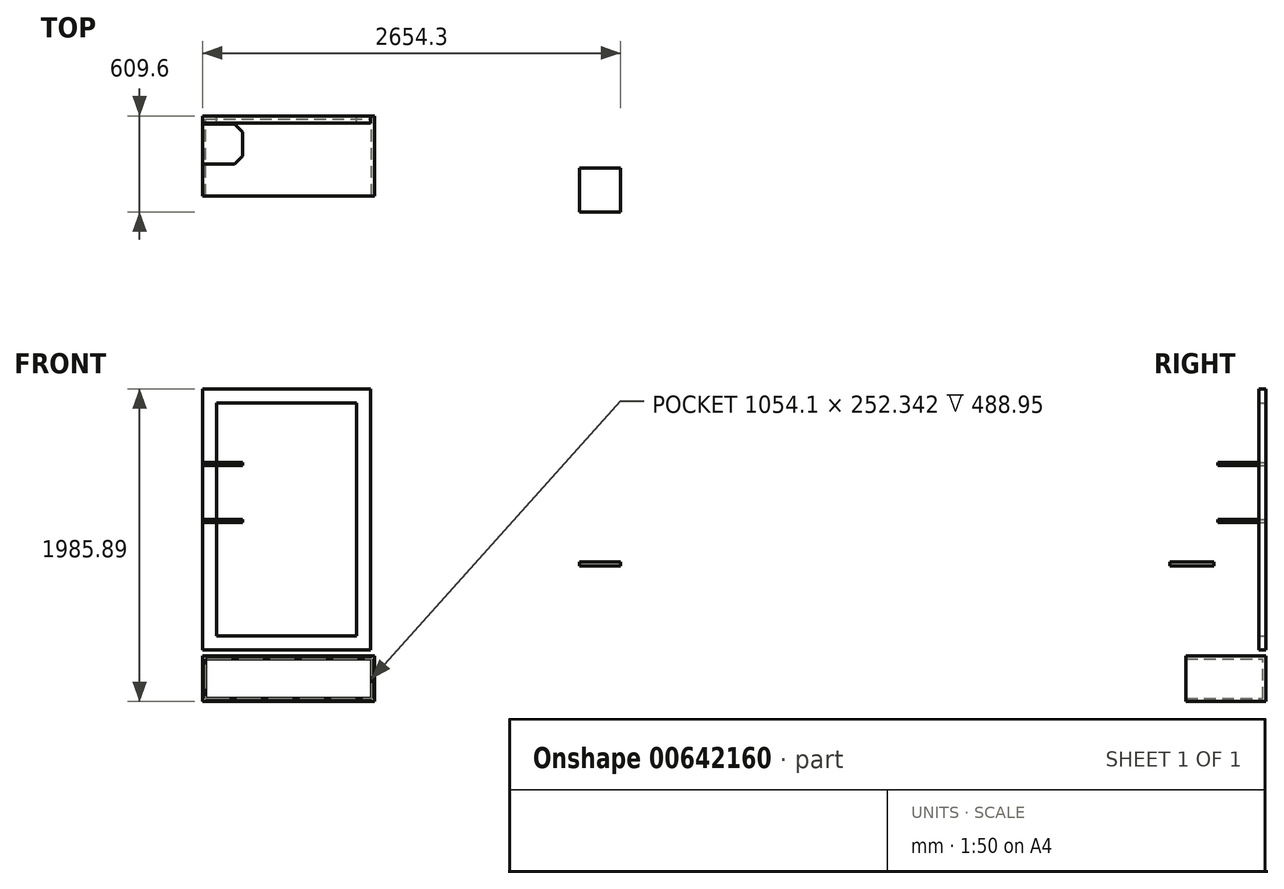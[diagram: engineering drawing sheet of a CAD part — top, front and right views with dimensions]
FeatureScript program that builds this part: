
annotation { "Feature Type Name" : "Feature", "Feature Type Description" : "" }
export const myFeature = defineFeature(function(context is Context, id is Id, definition is map)
    precondition{}
    {
        {
            var Q0;
            Q0=qCreatedBy(makeId("Front.planeOp"),FACE);
            var sketch = newSketch(context, id + "F0", { "sketchPlane" : qUnion([Q0])});
            skLineSegment(sketch, "E0.bottom", {"start": v(0, 0) * mm, "end": v(2654.3, 0) * mm});
            skLineSegment(sketch, "E0.top", {"start": v(0, 2432.05) * mm, "end": v(2654.3, 2432.05) * mm});
            skLineSegment(sketch, "E0.left", {"start": v(0, 0) * mm, "end": v(0, 2432.05) * mm});
            skLineSegment(sketch, "E0.right", {"start": v(2654.3, 0) * mm, "end": v(2654.3, 2432.05) * mm});
            skLineSegment(sketch, "E1.bottom", {"start": v(0, 495.3) * mm, "end": v(1066.8, 495.3) * mm});
            skLineSegment(sketch, "E1.top", {"start": v(0, 2152.65) * mm, "end": v(1066.8, 2152.65) * mm});
            skLineSegment(sketch, "E1.left", {"start": v(0, 495.3) * mm, "end": v(0, 2152.65) * mm});
            skLineSegment(sketch, "E1.right", {"start": v(1066.8, 495.3) * mm, "end": v(1066.8, 2152.65) * mm});
            skLineSegment(sketch, "E2.bottom", {"start": v(2654.3, 1029.79) * mm, "end": v(2393.58, 1029.79) * mm});
            skLineSegment(sketch, "E2.top", {"start": v(2654.3, 1065.5) * mm, "end": v(2393.58, 1065.5) * mm});
            skLineSegment(sketch, "E2.left", {"start": v(2654.3, 1029.79) * mm, "end": v(2654.3, 1065.5) * mm});
            skLineSegment(sketch, "E2.right", {"start": v(2393.58, 1029.79) * mm, "end": v(2393.58, 1065.5) * mm});
            skLineSegment(sketch, "E3.bottom", {"start": v(0, 0) * mm, "end": v(1092.2, 0) * mm});
            skLineSegment(sketch, "E3.top", {"start": v(0, 457.2) * mm, "end": v(1092.2, 457.2) * mm});
            skLineSegment(sketch, "E3.left", {"start": v(0, 0) * mm, "end": v(0, 457.2) * mm});
            skLineSegment(sketch, "E3.right", {"start": v(1092.2, 0) * mm, "end": v(1092.2, 457.2) * mm});
            skLineSegment(sketch, "E4", {"start": v(0, 166.76) * mm, "end": v(1092.2, 166.76) * mm});
            skLineSegment(sketch, "E5", {"start": v(1092.2, 0) * mm, "end": v(1092.2, 914.4) * mm});
            skLineSegment(sketch, "E6", {"start": v(1574.8, 1244.6) * mm, "end": v(1574.8, 0) * mm});
            skLineSegment(sketch, "E7", {"start": v(1981.2, 914.4) * mm, "end": v(1981.2, 0) * mm});
            skLineSegment(sketch, "E8", {"start": v(1574.8, 914.4) * mm, "end": v(1981.2, 914.4) * mm});
            skLineSegment(sketch, "E9", {"start": v(1574.8, 914.4) * mm, "end": v(1092.2, 914.4) * mm});
            skLineSegment(sketch, "E10", {"start": v(1092.2, 101.6) * mm, "end": v(1981.2, 101.6) * mm});
            skLineSegment(sketch, "E11", {"start": v(1981.2, 482.6) * mm, "end": v(2590.8, 482.6) * mm});
            skLineSegment(sketch, "E12", {"start": v(1981.2, 1054.41) * mm, "end": v(2590.8, 1054.41) * mm});
            skLineSegment(sketch, "E13", {"start": v(2590.8, 1054.41) * mm, "end": v(2654.3, 1054.41) * mm});
            skLineSegment(sketch, "E14.trimOffspring", {"start": v(2590.8, 1054.41) * mm, "end": v(2590.8, 0) * mm});
            skLineSegment(sketch, "E15", {"start": v(1574.8, 533.4) * mm, "end": v(1092.2, 533.4) * mm});
            skLineSegment(sketch, "E16", {"start": v(1981.2, 914.4) * mm, "end": v(1981.2, 1054.41) * mm});
            skLineSegment(sketch, "E17", {"start": v(1574.8, 1244.6) * mm, "end": v(1981.2, 1244.6) * mm});
            skLineSegment(sketch, "E18", {"start": v(1981.2, 1244.6) * mm, "end": v(1981.2, 1054.41) * mm});
            skLineSegment(sketch, "E19.bottom", {"start": v(0, 1687.02) * mm, "end": v(254, 1687.02) * mm});
            skLineSegment(sketch, "E19.top", {"start": v(0, 1667.97) * mm, "end": v(254, 1667.97) * mm});
            skLineSegment(sketch, "E19.left", {"start": v(0, 1687.02) * mm, "end": v(0, 1667.97) * mm});
            skLineSegment(sketch, "E19.right", {"start": v(254, 1687.02) * mm, "end": v(254, 1667.97) * mm});
            skLineSegment(sketch, "E20.bottom", {"start": v(0, 1323.98) * mm, "end": v(254, 1323.98) * mm});
            skLineSegment(sketch, "E20.top", {"start": v(0, 1304.93) * mm, "end": v(254, 1304.93) * mm});
            skLineSegment(sketch, "E20.left", {"start": v(0, 1323.98) * mm, "end": v(0, 1304.93) * mm});
            skLineSegment(sketch, "E20.right", {"start": v(254, 1323.98) * mm, "end": v(254, 1304.93) * mm});
            skLineSegment(sketch, "E21", {"start": v(1574.8, 355.6) * mm, "end": v(1981.2, 355.6) * mm});
            skLineSegment(sketch, "E22", {"start": v(88.9, 2063.75) * mm, "end": v(88.9, 584.2) * mm});
            skLineSegment(sketch, "E23", {"start": v(88.9, 2063.75) * mm, "end": v(977.9, 2063.75) * mm});
            skLineSegment(sketch, "E24", {"start": v(977.9, 2063.75) * mm, "end": v(977.9, 584.2) * mm});
            skLineSegment(sketch, "E25", {"start": v(88.9, 584.2) * mm, "end": v(977.9, 584.2) * mm});
            skSolve(sketch);
        }
        {
            var Q0;
            {var subQ4=sQuery(id+"F0.wireOp",EDGE,"E3.top");Q0=makeQuery(id+"F0.imprint","IMPRINT",FACE,{"disambiguationData":[TD([[makeQuery(id+"F0.imprint","IMPRINT",EDGE,{"derivedFrom":subQ4}),-1.0]])]});}
            extrude(context, id + "F1", {"entities" : qUnion([Q0]), "depth" : 508 * mm, "offsetDistance" : 25.4 * mm});
        }
        {
            var Q0;
            Q0=sQuery(id+"F0.wireOp",EDGE,"E5");
            var Q1;
            Q1=sQuery(id+"F0.wireOp",EDGE,"E6");
            var Q2;
            Q2=sQuery(id+"F0.wireOp",EDGE,"E16");
            var Q3;
            Q3=sQuery(id+"F0.wireOp",EDGE,"E7");
            var Q4;
            Q4=sQuery(id+"F0.wireOp",EDGE,"E14.trimOffspring");
            var Q5;
            Q5=sQuery(id+"F0.wireOp",EDGE,"E18");
            var Q6;
            Q6=sQuery(id+"F0.wireOp",EDGE,"sEqqkKkJ-zDKM-WJjd-21iw-gBiEN16Gd99Q");
            extrude(context, id + "F2", {"bodyType" : ToolBodyType.SURFACE, "surfaceEntities" : qUnion([Q0, Q1, Q2, Q3, Q4, Q5, Q6]), "depth" : 355.6 * mm, "offsetDistance" : 25.4 * mm});
        }
        {
            var Q0;
            Q0=sQuery(id+"F0.wireOp",EDGE,"Kjtz5eKt-ULTf-evfQ-Q5N2-FUeb1anu7QRw");
            var Q1;
            Q1=sQuery(id+"F0.wireOp",EDGE,"E9");
            var Q2;
            Q2=sQuery(id+"F0.wireOp",EDGE,"E8");
            var Q3;
            Q3=sQuery(id+"F0.wireOp",EDGE,"E12");
            var Q4;
            Q4=sQuery(id+"F0.wireOp",EDGE,"E11");
            var Q5;
            Q5=sQuery(id+"F0.wireOp",EDGE,"0XJa6nW8-y0aG-1m5H-tmE6-vHsM1P7Ta5Jt");
            var Q6;
            Q6=sQuery(id+"F0.wireOp",EDGE,"E15");
            var Q7;
            Q7=sQuery(id+"F0.wireOp",EDGE,"E10");
            var Q8;
            Q8=sQuery(id+"F0.wireOp",EDGE,"E17");
            var Q9;
            Q9=sQuery(id+"F0.wireOp",EDGE,"MFajBvlE-Buub-MDIa-xRfk-fOyj7VufqCmV");
            var Q10;
            Q10=sQuery(id+"F0.wireOp",EDGE,"E21");
            extrude(context, id + "F3", {"bodyType" : ToolBodyType.SURFACE, "surfaceEntities" : qUnion([Q0, Q1, Q2, Q3, Q4, Q5, Q6, Q7, Q8, Q9, Q10]), "depth" : 355.6 * mm, "offsetDistance" : 25.4 * mm});
        }
        {
            var Q0;
            Q0=sQuery(id+"F0.wireOp",EDGE,"E0.left");
            extrude(context, id + "F4", {"bodyType" : ToolBodyType.SURFACE, "surfaceEntities" : qUnion([Q0]), "depth" : 419.1 * mm, "offsetDistance" : 25.4 * mm});
        }
        {
            var Q0;
            Q0=sQuery(id+"F0.wireOp",EDGE,"E0.right");
            extrude(context, id + "F5", {"bodyType" : ToolBodyType.SURFACE, "surfaceEntities" : qUnion([Q0]), "depth" : 355.6 * mm, "offsetDistance" : 25.4 * mm});
        }
        {
            var Q0;
            Q0=makeQuery(id+"F0.imprint","IMPRINT",FACE,{"disambiguationData":[TD([[makeQuery(id+"F0.imprint","IMPRINT",EDGE,{"derivedFrom":sQuery(id+"F0.wireOp",EDGE,"E2.bottom")}),-1.0]])]});
            extrude(context, id + "F6", {"entities" : qUnion([Q0]), "depth" : 609.6 * mm, "offsetDistance" : 25.4 * mm, "hasSecondDirection" : true, "secondDirectionOppositeDirection" : false, "secondDirectionDepth" : 330.2 * mm});
        }
        {
            var Q0;
            Q0=makeQuery(id+"F0.imprint","IMPRINT",FACE,{"disambiguationData":[TD([[makeQuery(id+"F0.imprint","IMPRINT",EDGE,{"derivedFrom":sQuery(id+"F0.wireOp",EDGE,"E19.bottom")}),-1.0]])]});
            var Q1;
            Q1=makeQuery(id+"F0.imprint","IMPRINT",FACE,{"disambiguationData":[TD([[makeQuery(id+"F0.imprint","IMPRINT",EDGE,{"derivedFrom":sQuery(id+"F0.wireOp",EDGE,"E20.bottom")}),-1.0]])]});
            extrude(context, id + "F7", {"entities" : qUnion([Q0, Q1]), "depth" : 304.8 * mm, "offsetDistance" : 25.4 * mm, "hasSecondDirection" : true, "secondDirectionOppositeDirection" : false, "secondDirectionDepth" : 50.8 * mm});
        }
        {
            var Q0;
            Q0=makeQuery(id+"F7.opExtrude","CAP_EDGE",EDGE,{"disambiguationData":[OSD([sQuery(id+"F0.wireOp",EDGE,"E19.right")])],"isStart":false});
            var Q1;
            Q1=makeQuery(id+"F7.opExtrude","CAP_EDGE",EDGE,{"disambiguationData":[OSD([sQuery(id+"F0.wireOp",EDGE,"E20.right")])],"isStart":false});
            var Q2;
            Q2=makeQuery(id+"F7.opExtrude","CAP_EDGE",EDGE,{"disambiguationData":[OSD([sQuery(id+"F0.wireOp",EDGE,"E19.right")])],"isStart":true});
            var Q3;
            Q3=makeQuery(id+"F7.opExtrude","CAP_EDGE",EDGE,{"disambiguationData":[OSD([sQuery(id+"F0.wireOp",EDGE,"E20.right")])],"isStart":true});
            chamfer(context, id + "F8", {"entities" : qUnion([Q0, Q1, Q2, Q3]), "width" : 50.8 * mm, "tangentPropagation" : true});
        }
        {
            var Q0;
            {var subQ0=sQuery(id+"F0.wireOp",EDGE,"E20.left");Q0=makeQuery(id+"F0.imprint","IMPRINT",FACE,{"disambiguationData":[TD([[makeQuery(id+"F0.imprint","IMPRINT",EDGE,{"derivedFrom":subQ0}),1.0]])]});}
            var Q1;
            {var subQ0=sQuery(id+"F0.wireOp",EDGE,"E19.top");var subQ5=sQuery(id+"F0.wireOp",EDGE,"E22");var subQ7=makeQuery(id+"F0.imprint","INTERSECT",VERTEX,{"derivedFrom":[subQ0,subQ5]});Q1=makeQuery(id+"F0.imprint","IMPRINT",FACE,{"disambiguationData":[TD([[makeQuery(id+"F0.imprint","IMPRINT",EDGE,{"disambiguationData":[TD([[subQ7,-1.0]])],"derivedFrom":subQ5}),-1.0]])]});}
            var Q2;
            {var subQ0=sQuery(id+"F0.wireOp",EDGE,"E19.left");Q2=makeQuery(id+"F0.imprint","IMPRINT",FACE,{"disambiguationData":[TD([[makeQuery(id+"F0.imprint","IMPRINT",EDGE,{"derivedFrom":subQ0}),1.0]])]});}
            var Q3;
            {var subQ11=sQuery(id+"F0.wireOp",EDGE,"E1.bottom");Q3=makeQuery(id+"F0.imprint","IMPRINT",FACE,{"disambiguationData":[TD([[makeQuery(id+"F0.imprint","IMPRINT",EDGE,{"derivedFrom":subQ11}),1.0]])]});}
            extrude(context, id + "F9", {"entities" : qUnion([Q0, Q1, Q2, Q3]), "depth" : 44.45 * mm, "offsetDistance" : 25.4 * mm});
        }
        {
            var Q0;
            Q0=makeQuery(id+"F1.opExtrude","CAP_FACE",FACE,{"disambiguationData":[OSD([sQuery(id+"F0.wireOp",EDGE,"E3.top"),sQuery(id+"F0.wireOp",EDGE,"E3.left"),sQuery(id+"F0.wireOp",EDGE,"E4"),sQuery(id+"F0.wireOp",EDGE,"E5")])],"isStart":false});
            var Q1;
            Q1=makeQuery(id+"F1.opExtrude","SWEPT_BODY",BODY,{"disambiguationData":[OSD([sQuery(id+"F0.wireOp",EDGE,"E3.top"),sQuery(id+"F0.wireOp",EDGE,"E3.left"),sQuery(id+"F0.wireOp",EDGE,"E4"),sQuery(id+"F0.wireOp",EDGE,"E5")])]});
            shell(context, id + "F10", {"entities" : qUnion([Q0]), "parts" : qUnion([Q1]), "thickness" : 19.05 * mm});
        }
    });
